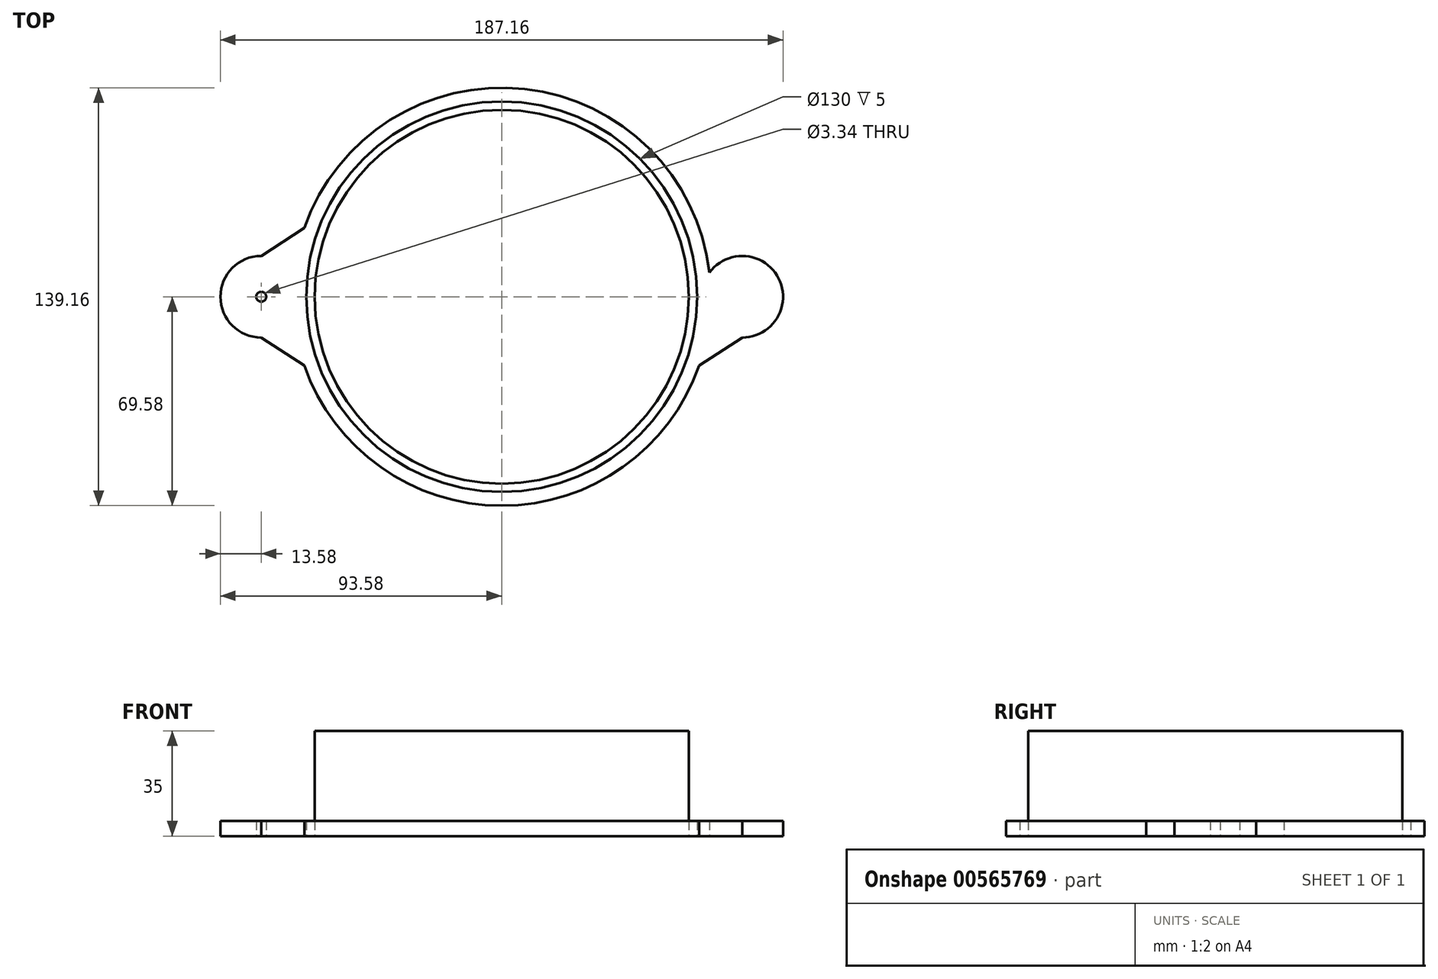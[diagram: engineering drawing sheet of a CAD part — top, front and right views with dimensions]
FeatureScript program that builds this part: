
annotation { "Feature Type Name" : "Feature", "Feature Type Description" : "" }
export const myFeature = defineFeature(function(context is Context, id is Id, definition is map)
    precondition{}
    {
        {
            var Q0;
            Q0=qCreatedBy(makeId("Top.planeOp"),FACE);
            var sketch = newSketch(context, id + "F0", { "sketchPlane" : qUnion([Q0])});
            skArc(sketch, "E0", {"start": v(65, 0) * mm, "mid": v(0, 65) * mm, "end": v(-65, 0) * mm});
            skArc(sketch, "E1", {"start": v(62.23, 0) * mm, "mid": v(0, 62.23) * mm, "end": v(-62.23, 0) * mm});
            skArc(sketch, "E2", {"start": v(-66.42, 0) * mm, "mid": v(-80, 13.58) * mm, "end": v(-93.58, 0) * mm});
            skLineSegment(sketch, "E3", {"start": v(-80, 13.58) * mm, "end": v(-59, 27.3) * mm});
            skLineSegment(sketch, "E4", {"start": v(-65, 0) * mm, "end": v(65, 0) * mm, "construction": true});
            skLineSegment(sketch, "E5", {"start": v(-66.42, 0) * mm, "end": v(-65, 0) * mm});
            skLineSegment(sketch, "E6", {"start": v(0, 65) * mm, "end": v(0, 0) * mm});
            skLineSegment(sketch, "E7", {"start": v(0, 62.23) * mm, "end": v(0, 0) * mm});
            skArc(sketch, "E8.MirrorCS", {"start": v(66.42, 0) * mm, "mid": v(80, 13.58) * mm, "end": v(93.58, 0) * mm});
            skLineSegment(sketch, "E9.MirrorCS", {"start": v(80, 13.58) * mm, "end": v(59, 27.3) * mm});
            skLineSegment(sketch, "E10", {"start": v(65, 0) * mm, "end": v(66.42, 0) * mm});
            skLineSegment(sketch, "E11.MirrorCS", {"start": v(-80, -13.58) * mm, "end": v(-59, -27.3) * mm});
            skLineSegment(sketch, "E12.MirrorCS", {"start": v(80, -13.58) * mm, "end": v(59, -27.3) * mm});
            skArc(sketch, "E13.MirrorCS", {"start": v(66.42, 0) * mm, "mid": v(80, -13.58) * mm, "end": v(93.58, 0) * mm});
            skArc(sketch, "E14.MirrorCS", {"start": v(65, 0) * mm, "mid": v(0, -65) * mm, "end": v(-65, 0) * mm});
            skArc(sketch, "E15.MirrorCS", {"start": v(62.23, 0) * mm, "mid": v(0, -62.23) * mm, "end": v(-62.23, 0) * mm});
            skArc(sketch, "E16.MirrorCS", {"start": v(-66.42, 0) * mm, "mid": v(-80, -13.58) * mm, "end": v(-93.58, 0) * mm});
            skCircle(sketch, "E17", {"center": v(-80, 0) * mm, "radius": 1.67 * mm});
            skCircle(sketch, "E18.MirrorC", {"center": v(80, 0) * mm, "radius": 1.67 * mm});
            skCircle(sketch, "E19", {"center": v(0, 0) * mm, "radius": 69.58 * mm});
            skSolve(sketch);
        }
        {
            var Q0;
            {var subQ1=sQuery(id+"F0.wireOp",EDGE,"E0");var subQ5=makeQuery(id+"F0.imprint","IMPRINT",VERTEX,{"derivedFrom":subQ1});Q0=makeQuery(id+"F0.imprint","IMPRINT",FACE,{"disambiguationData":[TD([[makeQuery(id+"F0.imprint","IMPRINT",EDGE,{"disambiguationData":[TD([[subQ5,1.0]])],"derivedFrom":subQ1}),-1.0]])]});}
            var Q1;
            {var subQ5=sQuery(id+"F0.wireOp",EDGE,"E5");Q1=makeQuery(id+"F0.imprint","IMPRINT",FACE,{"disambiguationData":[TD([[makeQuery(id+"F0.imprint","IMPRINT",EDGE,{"derivedFrom":subQ5}),1.0]])]});}
            var Q2;
            {var subQ1=sQuery(id+"F0.wireOp",EDGE,"E5");Q2=makeQuery(id+"F0.imprint","IMPRINT",FACE,{"disambiguationData":[TD([[makeQuery(id+"F0.imprint","IMPRINT",EDGE,{"derivedFrom":subQ1}),-1.0]])]});}
            var Q3;
            {var subQ0=sQuery(id+"F0.wireOp",EDGE,"E14.MirrorCS");var subQ1=sQuery(id+"F0.wireOp",EDGE,"E11.MirrorCS");var subQ2=makeQuery(id+"F0.imprint","INTERSECT",VERTEX,{"derivedFrom":[subQ1,subQ0]});Q3=makeQuery(id+"F0.imprint","IMPRINT",FACE,{"disambiguationData":[TD([[makeQuery(id+"F0.imprint","IMPRINT",EDGE,{"disambiguationData":[TD([[subQ2,1.0]])],"derivedFrom":subQ1}),-1.0]])]});}
            var Q4;
            {var subQ1=sQuery(id+"F0.wireOp",EDGE,"E10");Q4=makeQuery(id+"F0.imprint","IMPRINT",FACE,{"disambiguationData":[TD([[makeQuery(id+"F0.imprint","IMPRINT",EDGE,{"derivedFrom":subQ1}),-1.0]])]});}
            var Q5;
            {var subQ5=sQuery(id+"F0.wireOp",EDGE,"E10");Q5=makeQuery(id+"F0.imprint","IMPRINT",FACE,{"disambiguationData":[TD([[makeQuery(id+"F0.imprint","IMPRINT",EDGE,{"derivedFrom":subQ5}),1.0]])]});}
            var Q6;
            {var subQ1=sQuery(id+"F0.wireOp",EDGE,"E8.MirrorCS");var subQ3=sQuery(id+"F0.wireOp",EDGE,"E19");var subQ4=makeQuery(id+"F0.imprint","INTERSECT",VERTEX,{"derivedFrom":[subQ1,subQ3]});Q6=makeQuery(id+"F0.imprint","IMPRINT",FACE,{"disambiguationData":[TD([[makeQuery(id+"F0.imprint","IMPRINT",EDGE,{"disambiguationData":[TD([[subQ4,1.0]])],"derivedFrom":subQ3}),1.0]])]});}
            var Q7;
            {var subQ1=sQuery(id+"F0.wireOp",EDGE,"E2");var subQ3=sQuery(id+"F0.wireOp",EDGE,"E19");var subQ4=makeQuery(id+"F0.imprint","INTERSECT",VERTEX,{"derivedFrom":[subQ1,subQ3]});Q7=makeQuery(id+"F0.imprint","IMPRINT",FACE,{"disambiguationData":[TD([[makeQuery(id+"F0.imprint","IMPRINT",EDGE,{"disambiguationData":[TD([[subQ4,-1.0]])],"derivedFrom":subQ3}),1.0]])]});}
            extrude(context, id + "F1", {"entities" : qUnion([Q0, Q1, Q2, Q3, Q4, Q5, Q6, Q7]), "depth" : 5 * mm, "offsetDistance" : 25 * mm});
        }
        {
            var Q0;
            {var subQ0=sQuery(id+"F0.wireOp",EDGE,"E3");var subQ1=sQuery(id+"F0.wireOp",EDGE,"E2");var subQ2=makeQuery(id+"F0.imprint","INTERSECT",VERTEX,{"derivedFrom":[subQ1,subQ0]});Q0=makeQuery(id+"F0.imprint","IMPRINT",FACE,{"disambiguationData":[TD([[makeQuery(id+"F0.imprint","IMPRINT",EDGE,{"disambiguationData":[TD([[subQ2,1.0]])],"derivedFrom":subQ1}),-1.0]])]});}
            var Q1;
            Q1=makeQuery(id+"F0.imprint","IMPRINT",FACE,{"disambiguationData":[TD([[makeQuery(id+"F0.imprint","IMPRINT",EDGE,{"derivedFrom":sQuery(id+"F0.wireOp",EDGE,"E17")}),-1.0]])]});
            var Q2;
            {var subQ0=sQuery(id+"F0.wireOp",EDGE,"E16.MirrorCS");var subQ1=sQuery(id+"F0.wireOp",EDGE,"E11.MirrorCS");var subQ2=makeQuery(id+"F0.imprint","INTERSECT",VERTEX,{"derivedFrom":[subQ1,subQ0]});Q2=makeQuery(id+"F0.imprint","IMPRINT",FACE,{"disambiguationData":[TD([[makeQuery(id+"F0.imprint","IMPRINT",EDGE,{"disambiguationData":[TD([[subQ2,-1.0]])],"derivedFrom":subQ1}),1.0]])]});}
            var Q3;
            {var subQ0=sQuery(id+"F0.wireOp",EDGE,"E13.MirrorCS");var subQ1=sQuery(id+"F0.wireOp",EDGE,"E12.MirrorCS");var subQ2=makeQuery(id+"F0.imprint","INTERSECT",VERTEX,{"derivedFrom":[subQ1,subQ0]});Q3=makeQuery(id+"F0.imprint","IMPRINT",FACE,{"disambiguationData":[TD([[makeQuery(id+"F0.imprint","IMPRINT",EDGE,{"disambiguationData":[TD([[subQ2,-1.0]])],"derivedFrom":subQ1}),-1.0]])]});}
            var Q4;
            Q4=makeQuery(id+"F0.imprint","IMPRINT",FACE,{"disambiguationData":[TD([[makeQuery(id+"F0.imprint","IMPRINT",EDGE,{"derivedFrom":sQuery(id+"F0.wireOp",EDGE,"E18.MirrorC")}),1.0]])]});
            var Q5;
            {var subQ0=sQuery(id+"F0.wireOp",EDGE,"E9.MirrorCS");var subQ1=sQuery(id+"F0.wireOp",EDGE,"E8.MirrorCS");var subQ2=makeQuery(id+"F0.imprint","INTERSECT",VERTEX,{"derivedFrom":[subQ1,subQ0]});Q5=makeQuery(id+"F0.imprint","IMPRINT",FACE,{"disambiguationData":[TD([[makeQuery(id+"F0.imprint","IMPRINT",EDGE,{"disambiguationData":[TD([[subQ2,1.0]])],"derivedFrom":subQ1}),1.0]])]});}
            extrude(context, id + "F2", {"entities" : qUnion([Q0, Q1, Q2, Q3, Q4, Q5]), "operationType" : NewBodyOperationType.ADD, "depth" : 5 * mm, "offsetDistance" : 25 * mm});
        }
        {
            var Q0;
            {var subQ8=sQuery(id+"F0.wireOp",EDGE,"E15.MirrorCS");Q0=makeQuery(id+"F0.imprint","IMPRINT",FACE,{"disambiguationData":[TD([[makeQuery(id+"F0.imprint","IMPRINT",EDGE,{"derivedFrom":subQ8}),1.0]])]});}
            extrude(context, id + "F3", {"entities" : qUnion([Q0]), "operationType" : NewBodyOperationType.ADD, "depth" : 35 * mm, "offsetDistance" : 25 * mm});
        }
    });
